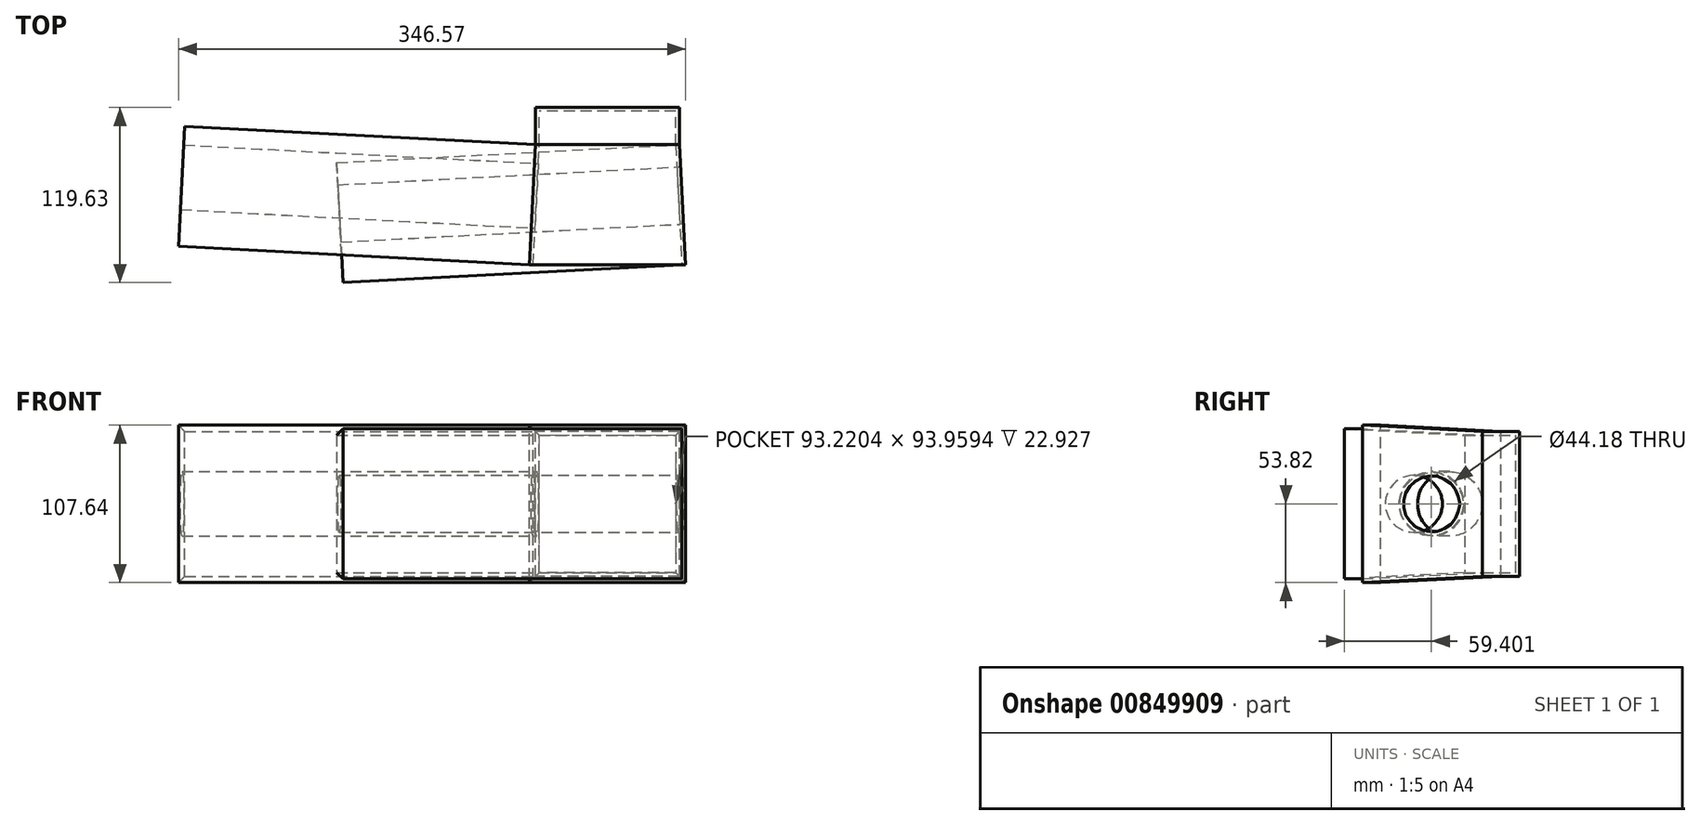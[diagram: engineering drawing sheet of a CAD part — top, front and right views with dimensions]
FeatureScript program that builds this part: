
annotation { "Feature Type Name" : "Feature", "Feature Type Description" : "" }
export const myFeature = defineFeature(function(context is Context, id is Id, definition is map)
    precondition{}
    {
        {
            var Q0;
            Q0=qCreatedBy(makeId("Front.planeOp"),FACE);
            var sketch = newSketch(context, id + "F0", { "sketchPlane" : qUnion([Q0])});
            skLineSegment(sketch, "E0.bottom", {"start": v(49.15, -49.52) * mm, "end": v(-49.15, -49.52) * mm});
            skLineSegment(sketch, "E0.top", {"start": v(49.15, 49.52) * mm, "end": v(-49.15, 49.52) * mm});
            skLineSegment(sketch, "E0.left", {"start": v(49.15, -49.52) * mm, "end": v(49.15, 49.52) * mm});
            skLineSegment(sketch, "E0.right", {"start": v(-49.15, -49.52) * mm, "end": v(-49.15, 49.52) * mm});
            skPoint(sketch, "E0.middle", {"position": v(0, 0) * mm});
            skSolve(sketch);
        }
        {
            var Q0;
            Q0 = qSketchRegion(id + "F0", true);
            extrude(context, id + "F1", {"entities" : qUnion([Q0]), "depth" : 82.1 * mm, "offsetDistance" : 25.4 * mm, "hasDraft" : true, "draftAngle" : 3 * degree, "hasSecondDirection" : true, "secondDirectionOppositeDirection" : true, "secondDirectionDepth" : 25.4 * mm});
        }
        {
            var Q0;
            Q0=makeQuery(id+"F1.opExtrude","CAP_FACE",FACE,{"disambiguationData":[OSD([sQuery(id+"F0.wireOp",EDGE,"E0.bottom"),sQuery(id+"F0.wireOp",EDGE,"E0.top"),sQuery(id+"F0.wireOp",EDGE,"E0.left"),sQuery(id+"F0.wireOp",EDGE,"E0.right")])],"isStart":false});
            shell(context, id + "F2", {"entities" : qUnion([Q0]), "thickness" : 2.54 * mm});
        }
        {
            var Q0;
            Q0=qCreatedBy(makeId("Right.planeOp"),FACE);
            var sketch = newSketch(context, id + "F3", { "sketchPlane" : qUnion([Q0])});
            skCircle(sketch, "E1", {"center": v(-34.83, 0) * mm, "radius": 22.09 * mm});
            skSolve(sketch);
        }
        {
            var Q0;
            Q0 = qSketchRegion(id + "F3", true);
            extrude(context, id + "F4", {"entities" : qUnion([Q0]), "operationType" : NewBodyOperationType.REMOVE, "oppositeDirection" : true, "depth" : 137.98 * mm, "offsetDistance" : 25.4 * mm, "hasSecondDirection" : true, "secondDirectionOppositeDirection" : false, "secondDirectionDepth" : 94.6 * mm, "hasSecondDirectionDraft" : true, "secondDirectionDraftAngle" : 3 * degree, "secondDirectionDraftPullDirection" : true});
        }
        {
            var Q0;
            {var subQ0=sQuery(id+"F0.wireOp",EDGE,"E0.left");Q0=makeQuery(id+"F2.opShell","OFFSET_FACE",FACE,{"disambiguationData":[OSD([subQ0]),TDD([makeQuery(id+"F1.*.split.splitOp","SPLIT",FACE,{"derivedFrom":makeQuery(id+"F1.opExtrude","SWEPT_FACE",FACE,{"disambiguationData":[OSD([subQ0])]})})])]});}
            extrude(context, id + "F5", {"entities" : qUnion([Q0]), "depth" : 232 * mm, "offsetDistance" : 25.4 * mm});
        }
        {
            var Q0;
            Q0=makeQuery(id+"F1.*.split.splitOp","SPLIT",FACE,{"derivedFrom":makeQuery(id+"F1.opExtrude","SWEPT_FACE",FACE,{"disambiguationData":[OSD([sQuery(id+"F0.wireOp",EDGE,"E0.right")])]})});
            extrude(context, id + "F6", {"entities" : qUnion([Q0]), "depth" : 240 * mm, "offsetDistance" : 25.4 * mm});
        }
    });
